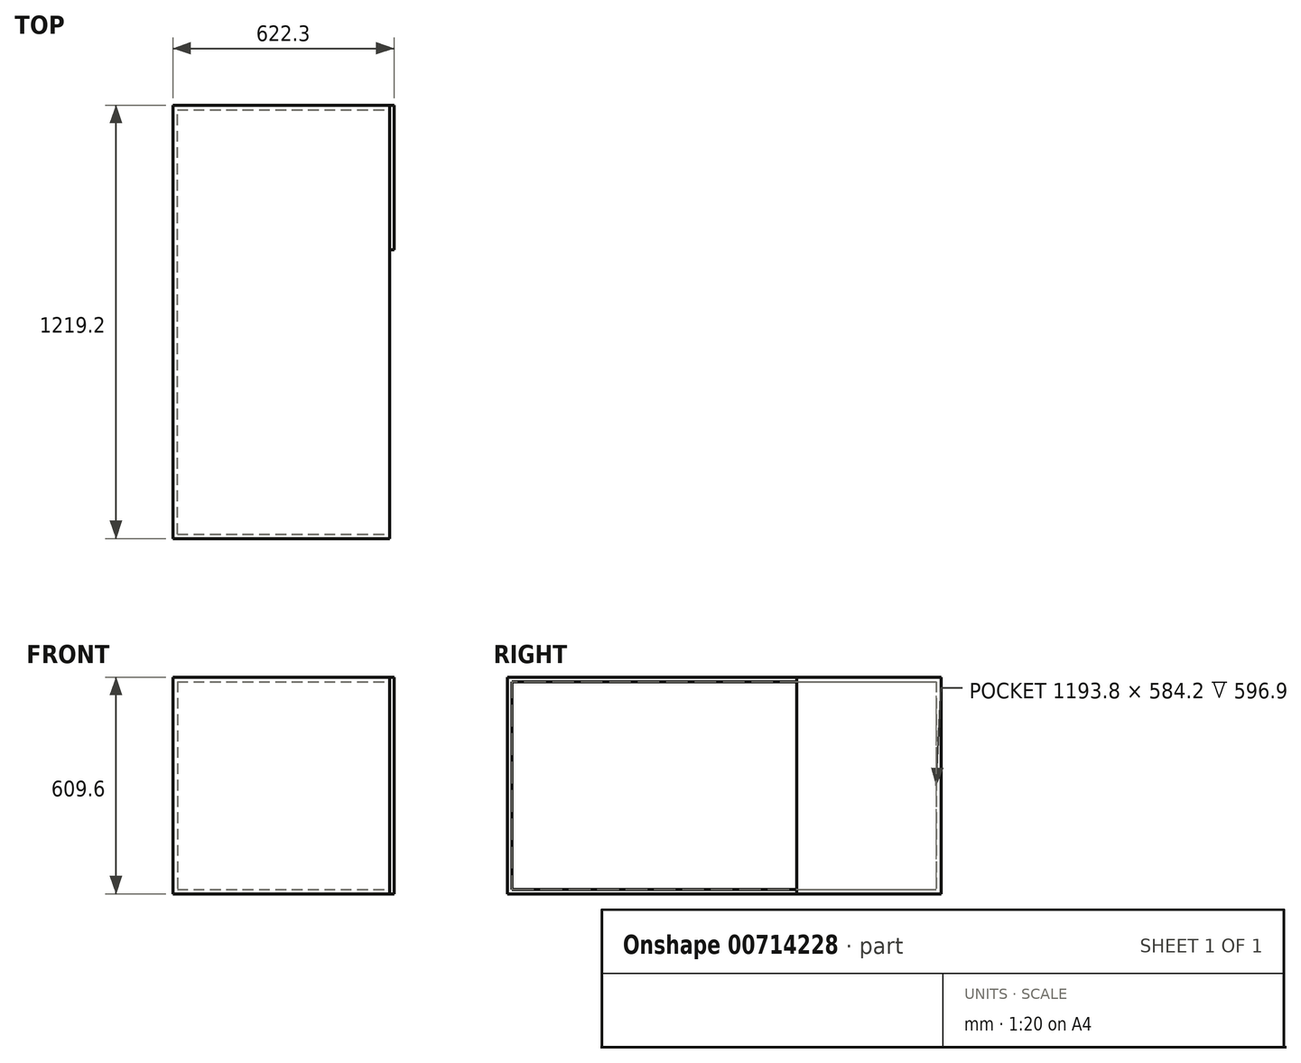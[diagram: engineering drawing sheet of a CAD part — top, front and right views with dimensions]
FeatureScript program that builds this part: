
annotation { "Feature Type Name" : "Feature", "Feature Type Description" : "" }
export const myFeature = defineFeature(function(context is Context, id is Id, definition is map)
    precondition{}
    {
        {
            var Q0;
            Q0=qCreatedBy(makeId("Right.planeOp"),FACE);
            var sketch = newSketch(context, id + "F0", { "sketchPlane" : qUnion([Q0])});
            skLineSegment(sketch, "E0.bottom", {"start": v(-615.9, 356.51) * mm, "end": v(603.3, 356.51) * mm});
            skLineSegment(sketch, "E0.top", {"start": v(-615.9, -253.09) * mm, "end": v(603.3, -253.09) * mm});
            skLineSegment(sketch, "E0.left", {"start": v(-615.9, 356.51) * mm, "end": v(-615.9, -253.09) * mm});
            skLineSegment(sketch, "E0.right", {"start": v(603.3, 356.51) * mm, "end": v(603.3, -253.09) * mm});
            skSolve(sketch);
        }
        {
            var Q0;
            Q0=makeQuery(id+"F0.imprint","IMPRINT",FACE,{"disambiguationData":[TD([[makeQuery(id+"F0.imprint","IMPRINT",EDGE,{"derivedFrom":sQuery(id+"F0.wireOp",EDGE,"E0.bottom")}),-1.0]])]});
            extrude(context, id + "F1", {"entities" : qUnion([Q0]), "depth" : 609.6 * mm, "offsetDistance" : 25.4 * mm});
        }
        {
            var Q0;
            Q0=makeQuery(id+"F1.opExtrude","CAP_FACE",FACE,{"disambiguationData":[OSD([sQuery(id+"F0.wireOp",EDGE,"E0.bottom"),sQuery(id+"F0.wireOp",EDGE,"E0.top"),sQuery(id+"F0.wireOp",EDGE,"E0.left"),sQuery(id+"F0.wireOp",EDGE,"E0.right")])],"isStart":false});
            var sketch = newSketch(context, id + "F2", { "sketchPlane" : qUnion([Q0])});
            skLineSegment(sketch, "E1.0", {"start": v(-603.2, 343.81) * mm, "end": v(590.6, 343.81) * mm});
            skLineSegment(sketch, "E1.1", {"start": v(-603.2, 343.81) * mm, "end": v(-603.2, -240.39) * mm});
            skLineSegment(sketch, "E1.2", {"start": v(-603.2, -240.39) * mm, "end": v(590.6, -240.39) * mm});
            skLineSegment(sketch, "E1.3", {"start": v(590.6, 343.81) * mm, "end": v(590.6, -240.39) * mm});
            skSolve(sketch);
        }
        {
            var Q0;
            Q0=makeQuery(id+"F2.imprint","IMPRINT",FACE,{"disambiguationData":[TD([[makeQuery(id+"F2.imprint","IMPRINT",EDGE,{"derivedFrom":sQuery(id+"F2.wireOp",EDGE,"E1.0")}),-1.0]])]});
            extrude(context, id + "F3", {"entities" : qUnion([Q0]), "operationType" : NewBodyOperationType.REMOVE, "oppositeDirection" : true, "depth" : 596.9 * mm, "offsetDistance" : 25.4 * mm});
        }
        {
            var Q0;
            Q0=makeQuery(id+"F1.opExtrude","CAP_FACE",FACE,{"disambiguationData":[OSD([sQuery(id+"F0.wireOp",EDGE,"E0.bottom"),sQuery(id+"F0.wireOp",EDGE,"E0.top"),sQuery(id+"F0.wireOp",EDGE,"E0.left"),sQuery(id+"F0.wireOp",EDGE,"E0.right")])],"isStart":false});
            var sketch = newSketch(context, id + "F4", { "sketchPlane" : qUnion([Q0])});
            skLineSegment(sketch, "E2.bottom", {"start": v(603.3, -253.09) * mm, "end": v(196.9, -253.09) * mm});
            skLineSegment(sketch, "E2.top", {"start": v(603.3, 356.51) * mm, "end": v(196.9, 356.51) * mm});
            skLineSegment(sketch, "E2.left", {"start": v(603.3, -253.09) * mm, "end": v(603.3, 356.51) * mm});
            skLineSegment(sketch, "E2.right", {"start": v(196.9, -253.09) * mm, "end": v(196.9, 356.51) * mm});
            skSolve(sketch);
        }
        {
            var Q0;
            Q0 = qSketchRegion(id + "F4", true);
            extrude(context, id + "F5", {"entities" : qUnion([Q0]), "depth" : 12.7 * mm, "offsetDistance" : 25.4 * mm});
        }
    });
